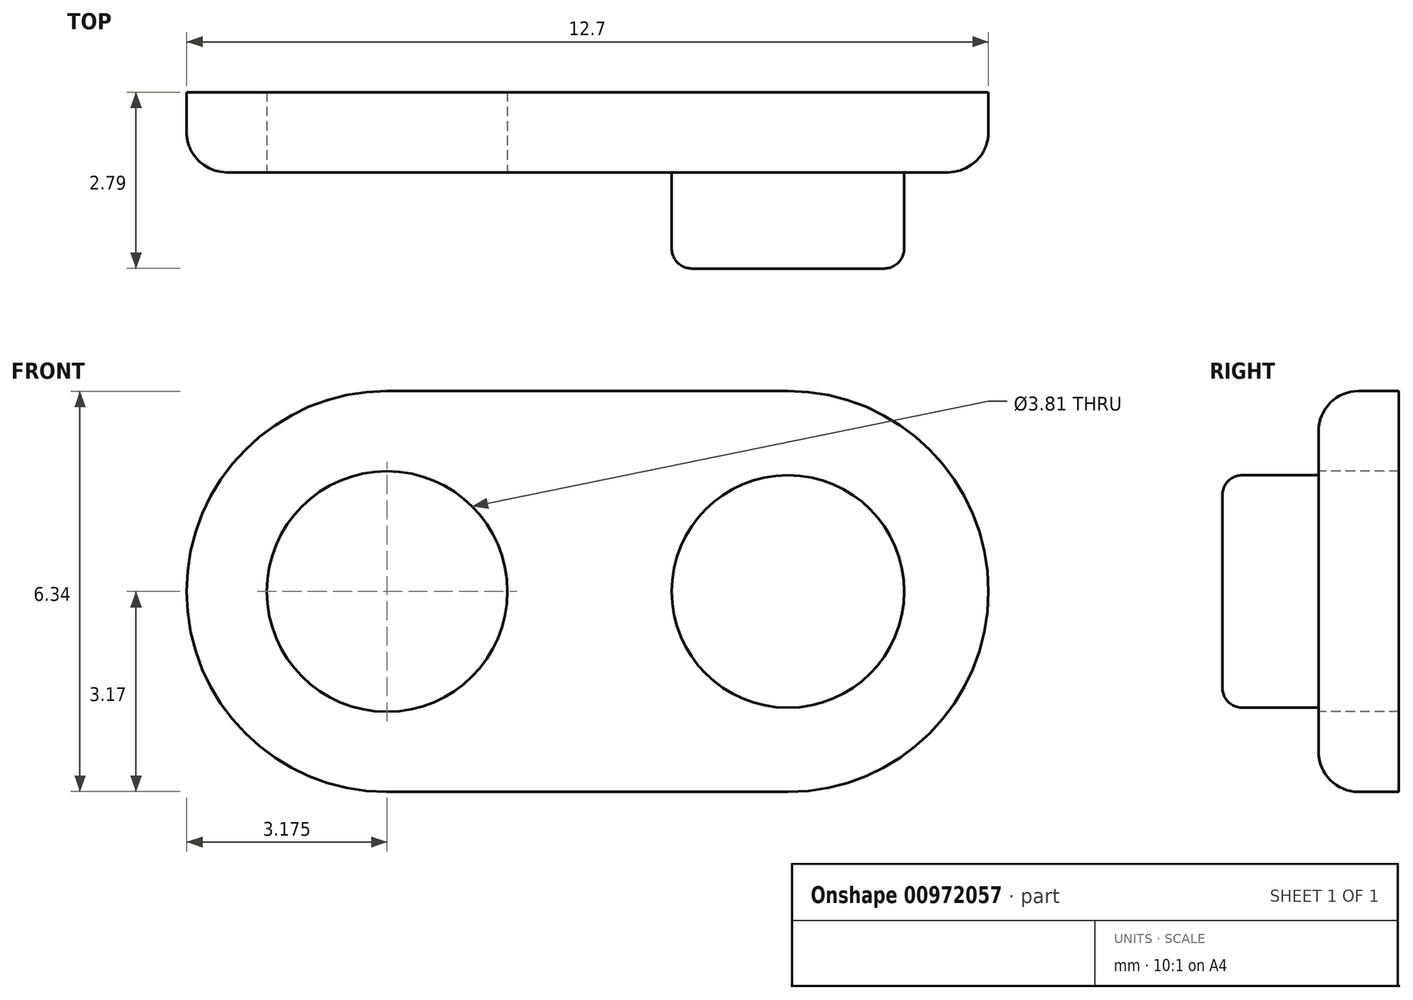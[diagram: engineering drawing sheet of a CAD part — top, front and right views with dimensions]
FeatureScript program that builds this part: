
annotation { "Feature Type Name" : "Feature", "Feature Type Description" : "" }
export const myFeature = defineFeature(function(context is Context, id is Id, definition is map)
    precondition{}
    {
        {
            var Q0;
            Q0=qCreatedBy(makeId("Front.planeOp"),FACE);
            var sketch = newSketch(context, id + "F0", { "sketchPlane" : qUnion([Q0])});
            skPoint(sketch, "E0", {"position": v(-3.18, 0) * mm});
            skPoint(sketch, "E1", {"position": v(3.18, 0) * mm});
            skCircle(sketch, "E2", {"center": v(-3.18, 0) * mm, "radius": 3.18 * mm});
            skCircle(sketch, "E3", {"center": v(3.18, 0) * mm, "radius": 3.18 * mm});
            skLineSegment(sketch, "E4", {"start": v(-3.18, 3.18) * mm, "end": v(3.18, 3.18) * mm});
            skLineSegment(sketch, "E5", {"start": v(-3.18, -3.18) * mm, "end": v(3.18, -3.17) * mm});
            skSolve(sketch);
        }
        {
            var Q0;
            {var subQ0=sQuery(id+"F0.wireOp",EDGE,"E3");var subQ1=makeQuery(id+"F0.imprint","INTERSECT",VERTEX,{"derivedFrom":[subQ0,sQuery(id+"F0.wireOp",EDGE,"E4")]});Q0=makeQuery(id+"F0.imprint","IMPRINT",FACE,{"disambiguationData":[TD([[makeQuery(id+"F0.imprint","IMPRINT",EDGE,{"disambiguationData":[TD([[subQ1,-1.0]])],"derivedFrom":subQ0}),1.0]])]});}
            var Q1;
            {var subQ0=sQuery(id+"F0.wireOp",EDGE,"E5");Q1=makeQuery(id+"F0.imprint","IMPRINT",FACE,{"disambiguationData":[TD([[makeQuery(id+"F0.imprint","IMPRINT",EDGE,{"derivedFrom":subQ0}),1.0]])]});}
            var Q2;
            {var subQ0=sQuery(id+"F0.wireOp",EDGE,"E2");var subQ1=makeQuery(id+"F0.imprint","INTERSECT",VERTEX,{"derivedFrom":[subQ0,sQuery(id+"F0.wireOp",EDGE,"E4")]});Q2=makeQuery(id+"F0.imprint","IMPRINT",FACE,{"disambiguationData":[TD([[makeQuery(id+"F0.imprint","IMPRINT",EDGE,{"disambiguationData":[TD([[subQ1,1.0]])],"derivedFrom":subQ0}),1.0]])]});}
            var Q3;
            {var subQ0=sQuery(id+"F0.wireOp",EDGE,"E4");Q3=makeQuery(id+"F0.imprint","IMPRINT",FACE,{"disambiguationData":[TD([[makeQuery(id+"F0.imprint","IMPRINT",EDGE,{"derivedFrom":subQ0}),-1.0]])]});}
            extrude(context, id + "F1", {"entities" : qUnion([Q0, Q1, Q2, Q3]), "depth" : 1.27 * mm, "offsetDistance" : 25.4 * mm});
        }
        {
            var Q0;
            Q0=makeQuery(id+"F1.opExtrude","CAP_EDGE",EDGE,{"disambiguationData":[OSD([sQuery(id+"F0.wireOp",EDGE,"E4")])],"isStart":false});
            var Q1;
            Q1=makeQuery(id+"F1.opExtrude","CAP_EDGE",EDGE,{"disambiguationData":[OSD([sQuery(id+"F0.wireOp",EDGE,"E2")])],"isStart":false});
            var Q2;
            Q2=makeQuery(id+"F1.opExtrude","CAP_EDGE",EDGE,{"disambiguationData":[OSD([sQuery(id+"F0.wireOp",EDGE,"E3")])],"isStart":false});
            var Q3;
            Q3=makeQuery(id+"F1.opExtrude","CAP_EDGE",EDGE,{"disambiguationData":[OSD([sQuery(id+"F0.wireOp",EDGE,"E5")])],"isStart":false});
            fillet(context, id + "F2", {"entities" : qUnion([Q0, Q1, Q2, Q3]), "radius" : 0.64 * mm, "tangentPropagation" : true, "allowEdgeOverflow" : false});
        }
        {
            var Q0;
            Q0=makeQuery(id+"F1.opExtrude","CAP_FACE",FACE,{"disambiguationData":[OSD([sQuery(id+"F0.wireOp",EDGE,"E2"),sQuery(id+"F0.wireOp",EDGE,"E3"),sQuery(id+"F0.wireOp",EDGE,"E4"),sQuery(id+"F0.wireOp",EDGE,"E5")])],"isStart":false});
            var sketch = newSketch(context, id + "F3", { "sketchPlane" : qUnion([Q0])});
            skPoint(sketch, "E6", {"position": v(0, 0) * mm});
            skSolve(sketch);
        }
        {
            var Q0;
            {var subQ0=sQuery(id+"F0.wireOp",EDGE,"E5");var subQ1=sQuery(id+"F0.wireOp",EDGE,"E4");var subQ2=sQuery(id+"F0.wireOp",EDGE,"E3");var subQ3=sQuery(id+"F0.wireOp",EDGE,"E2");var subQ4=makeQuery(id+"F1.opExtrude","CAP_FACE",FACE,{"disambiguationData":[OSD([subQ3,subQ2,subQ1,subQ0])],"isStart":false});Q0=makeQuery(id+"F3.imprint","IMPRINT",FACE,{"disambiguationData":[TD([[makeQuery(id+"F3.imprint","IMPRINT",EDGE,{"derivedFrom":makeQuery(id+"F2.opFillet","BLEND_EDGE",EDGE,{"blendedFrom":[makeQuery(id+"F1.opExtrude","CAP_EDGE",EDGE,{"disambiguationData":[OSD([subQ3])],"isStart":false}),subQ4],"blendedInto":[subQ4]})}),1.0]])]});}
            var sketch = newSketch(context, id + "F4", { "sketchPlane" : qUnion([Q0])});
            skPoint(sketch, "E7", {"position": v(3.18, 0) * mm});
            skCircle(sketch, "E8", {"center": v(3.18, 0) * mm, "radius": 1.84 * mm});
            skPoint(sketch, "E9", {"position": v(0, 0) * mm});
            skSolve(sketch);
        }
        {
            var Q0;
            Q0=makeQuery(id+"F4.imprint","IMPRINT",FACE,{"disambiguationData":[TD([[makeQuery(id+"F4.imprint","IMPRINT",EDGE,{"derivedFrom":sQuery(id+"F4.wireOp",EDGE,"E8")}),1.0]])]});
            extrude(context, id + "F5", {"entities" : qUnion([Q0]), "operationType" : NewBodyOperationType.ADD, "depth" : 1.52 * mm, "offsetDistance" : 25.4 * mm});
        }
        {
            var Q0;
            {var subQ0=sQuery(id+"F0.wireOp",EDGE,"E5");var subQ1=sQuery(id+"F0.wireOp",EDGE,"E4");var subQ2=sQuery(id+"F0.wireOp",EDGE,"E3");var subQ3=sQuery(id+"F0.wireOp",EDGE,"E2");var subQ4=makeQuery(id+"F1.opExtrude","CAP_FACE",FACE,{"disambiguationData":[OSD([subQ3,subQ2,subQ1,subQ0])],"isStart":false});Q0=makeQuery(id+"F3.imprint","IMPRINT",FACE,{"disambiguationData":[TD([[makeQuery(id+"F3.imprint","IMPRINT",EDGE,{"derivedFrom":makeQuery(id+"F2.opFillet","BLEND_EDGE",EDGE,{"blendedFrom":[makeQuery(id+"F1.opExtrude","CAP_EDGE",EDGE,{"disambiguationData":[OSD([subQ3])],"isStart":false}),subQ4],"blendedInto":[subQ4]})}),1.0]])]});}
            var sketch = newSketch(context, id + "F6", { "sketchPlane" : qUnion([Q0])});
            skPoint(sketch, "E10", {"position": v(-3.18, 0) * mm});
            skSolve(sketch);
        }
        {
            var Q0;
            Q0=sQuery(id+"F6.wireOp",VERTEX,"E10");
            var Q1;
            Q1=makeQuery(id+"F1.opExtrude","SWEPT_BODY",BODY,{"disambiguationData":[OSD([sQuery(id+"F0.wireOp",EDGE,"E2"),sQuery(id+"F0.wireOp",EDGE,"E3"),sQuery(id+"F0.wireOp",EDGE,"E4"),sQuery(id+"F0.wireOp",EDGE,"E5")])]});
            hole(context, id + "F7", {"style" : HoleStyle.SIMPLE, "endStyle" : HoleEndStyle.THROUGH, "holeDiameter" : 3.8 * mm, "majorDiameter" : 6.35 * mm, "isTappedThrough" : true, "tappedDepth" : 12.7 * mm, "tapClearance" : 3, "locations" : qUnion([Q0]), "scope" : qUnion([Q1])});
        }
        {
            var Q0;
            Q0=makeQuery(id+"F5.opExtrude","CAP_EDGE",EDGE,{"disambiguationData":[OSD([sQuery(id+"F4.wireOp",EDGE,"E8")])],"isStart":false});
            fillet(context, id + "F8", {"entities" : qUnion([Q0]), "radius" : 0.32 * mm, "tangentPropagation" : true, "allowEdgeOverflow" : false});
        }
    });
